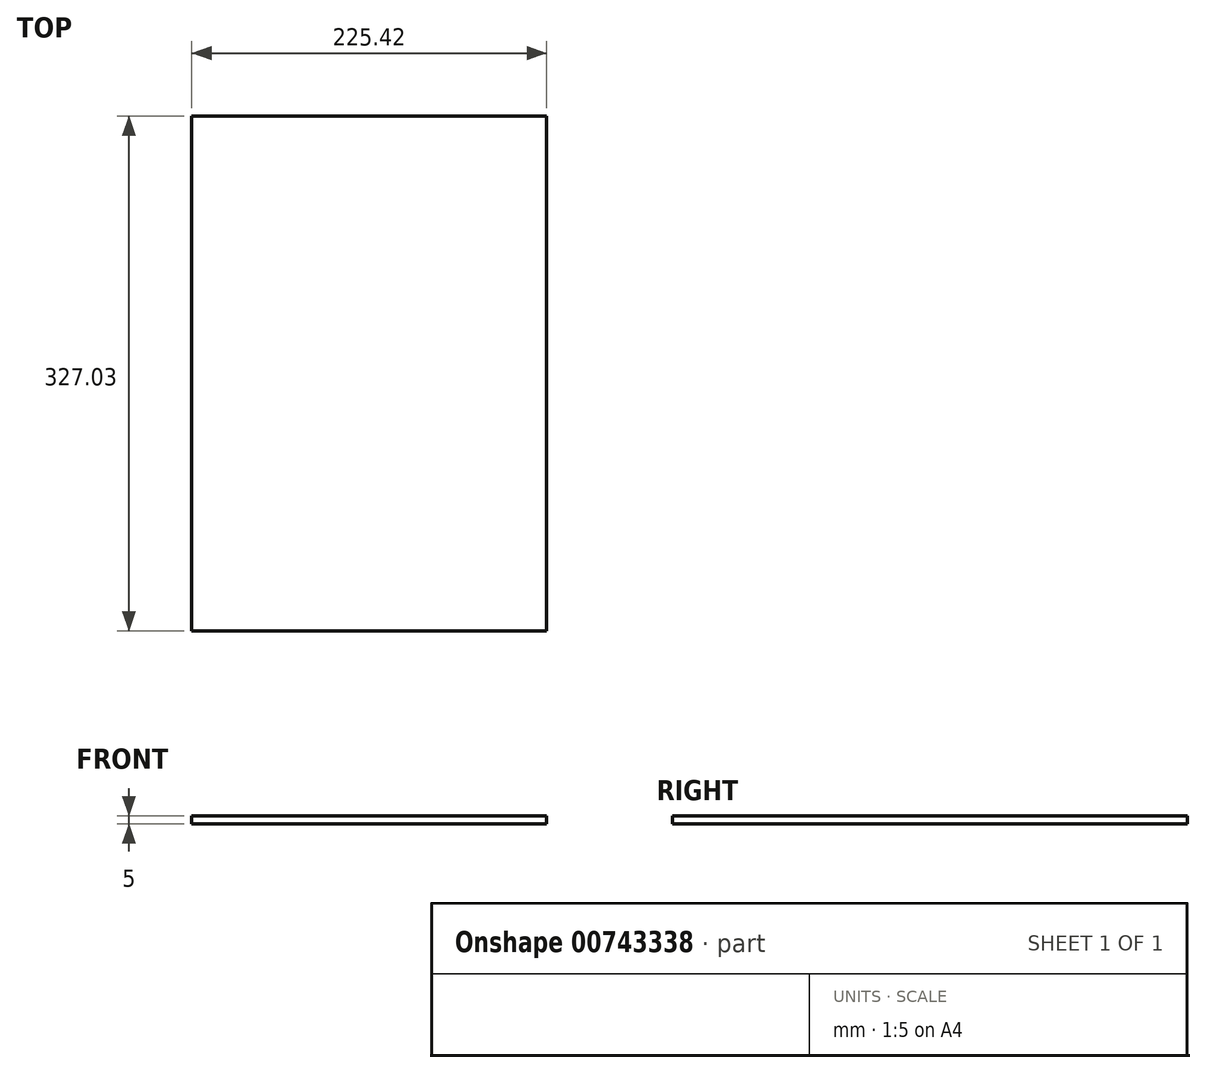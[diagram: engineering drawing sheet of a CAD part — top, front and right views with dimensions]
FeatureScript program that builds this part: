
annotation { "Feature Type Name" : "Feature", "Feature Type Description" : "" }
export const myFeature = defineFeature(function(context is Context, id is Id, definition is map)
    precondition{}
    {
        {
            var Q0;
            Q0=qCreatedBy(makeId("Top.planeOp"),FACE);
            var sketch = newSketch(context, id + "F0", { "sketchPlane" : qUnion([Q0])});
            skLineSegment(sketch, "E0.bottom", {"start": v(0, 0) * mm, "end": v(225.43, 0) * mm});
            skLineSegment(sketch, "E0.top", {"start": v(0, 327.02) * mm, "end": v(225.42, 327.02) * mm});
            skLineSegment(sketch, "E0.left", {"start": v(0, 0) * mm, "end": v(0, 327.02) * mm});
            skLineSegment(sketch, "E0.right", {"start": v(225.43, 0) * mm, "end": v(225.43, 327.02) * mm});
            skSolve(sketch);
        }
        {
            var Q0;
            Q0 = qSketchRegion(id + "F0", true);
            extrude(context, id + "F1", {"entities" : qUnion([Q0]), "depth" : 5 * mm, "offsetDistance" : 25 * mm});
        }
    });
